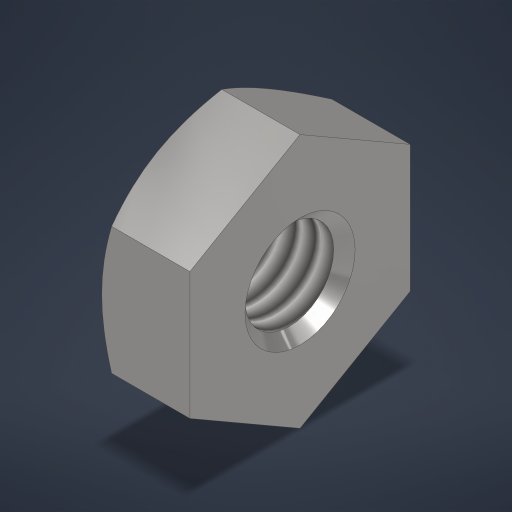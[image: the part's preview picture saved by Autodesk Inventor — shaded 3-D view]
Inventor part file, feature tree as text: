
AUTODESK INVENTOR PART (.ipt)
format: ipt  version: 2023.3 (Build 273359000, 359)  size: 233,984 bytes
history: native  units: mm
features: other x14, sketch x3, revolve x2, thread x1, extrude x1
ambient origin geometry x8: Origin, YZ Plane, XZ Plane, XY Plane, X Axis, Y Axis, Z Axis, Center Point
bodies: Solid1 (feature_tree)
feature tree (21):
  revolve  "Revolution1"  Angle=360.0deg
  revolve  "Revolution2"  [1 undecoded]
  thread  "Thread1"  [1 undecoded]
  extrude  "Extrusion1"  [1 undecoded]
  other  "cp_XY"
  other  "cp_YZ"
  other  "cp_ZX"
  other  "cp_X"
  other  "cp_Y"
  other  "cp_Z"
  other  "cp_Center"
  other  "nut_to_screw_XY"
  other  "nut_to_screw_YZ"
  other  "nut_to_screw_ZX"
  other  "nut_to_screw_X"
  other  "nut_to_screw_Y"
  other  "nut_to_screw_Z"
  other  "nut_to_screw_Center"
  sketch  "Sketch_1"  dims[d0=360.0deg d1=360.0deg]
  sketch  "Sketch_2"  dims[d2=1.513mm d3=0.0mm d4=2.0mm d5=0.0mm d6=0.0mm]
  sketch  "Sketch_3"
note: 3 required parameter values undecoded (feature->parameter linkage not recoverable at this tier; creation-order binding heuristic only, values carry confidence <= 0.55)